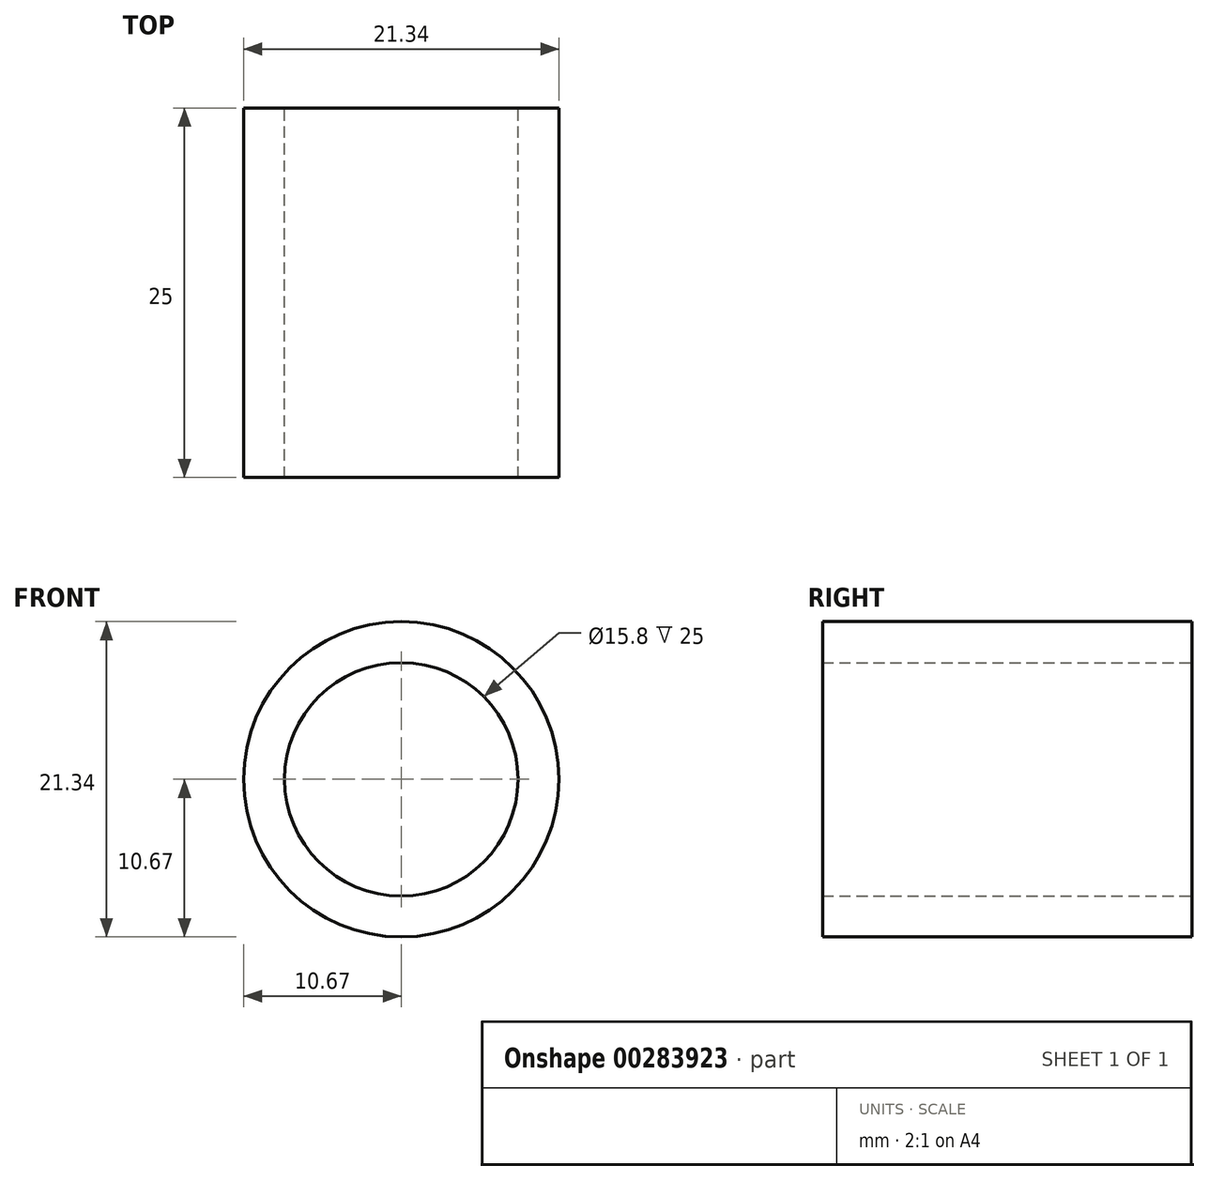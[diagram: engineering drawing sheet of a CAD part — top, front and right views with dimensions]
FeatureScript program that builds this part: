
annotation { "Feature Type Name" : "Feature", "Feature Type Description" : "" }
export const myFeature = defineFeature(function(context is Context, id is Id, definition is map)
    precondition{}
    {
        {
            var Q0;
            Q0=qCreatedBy(makeId("Front.planeOp"),FACE);
            var sketch = newSketch(context, id + "F0", { "sketchPlane" : qUnion([Q0])});
            skCircle(sketch, "E0", {"center": v(0, 0) * mm, "radius": 7.9 * mm});
            skCircle(sketch, "E1", {"center": v(0, 0) * mm, "radius": 10.67 * mm});
            skSolve(sketch);
        }
        {
            var Q0;
            Q0 = qSketchRegion(id + "F0", true);
            extrude(context, id + "F1", {"entities" : qUnion([Q0]), "endBound" : BoundingType.SYMMETRIC, "depth" : 25 * mm});
        }
    });
